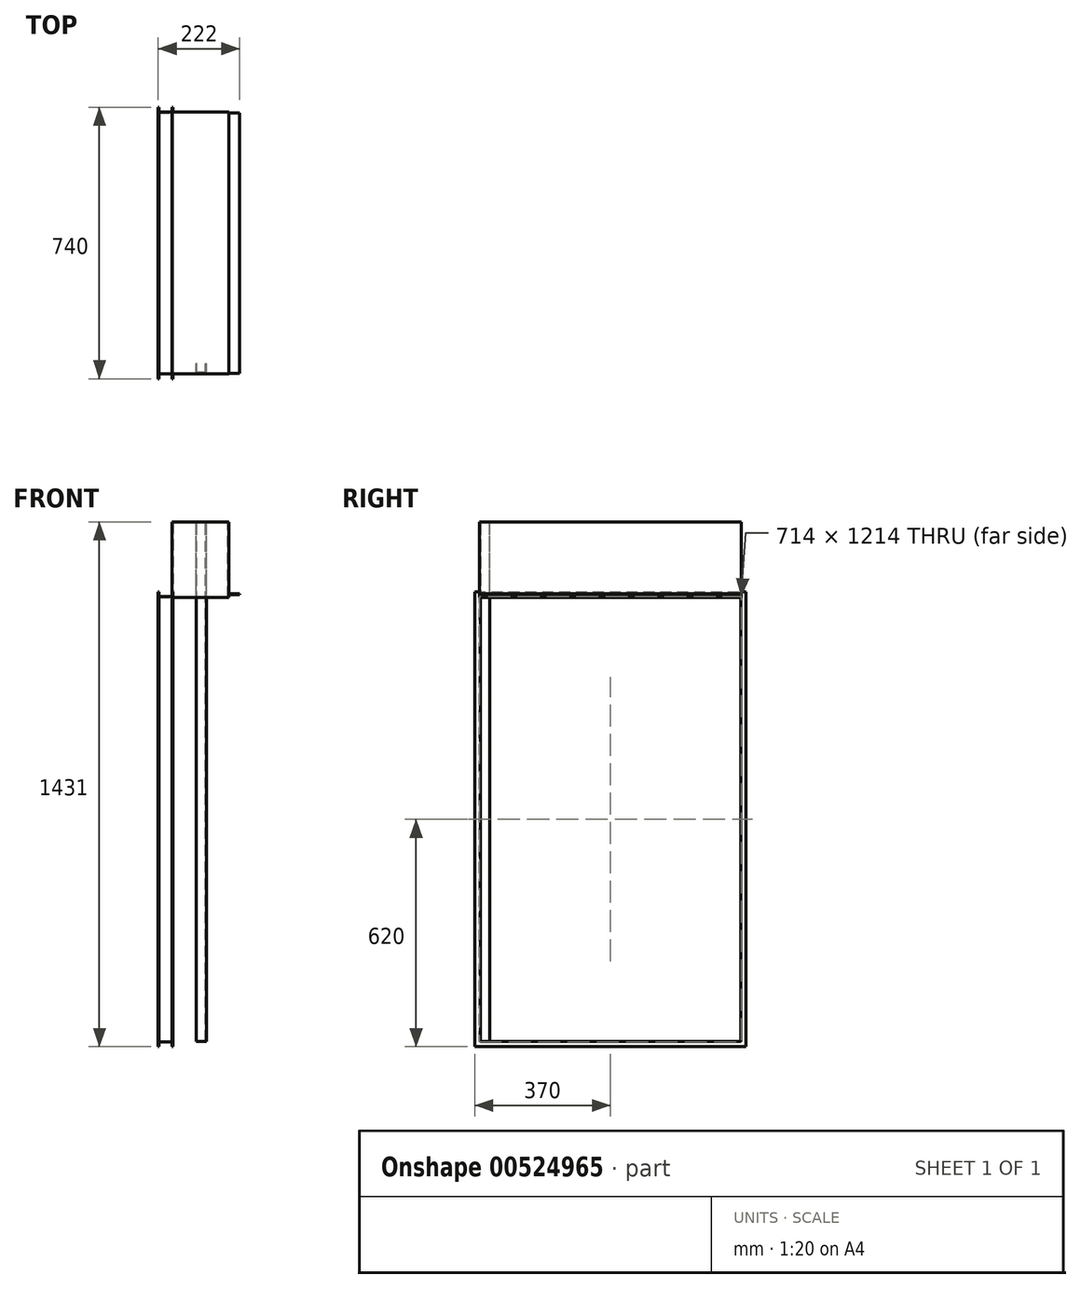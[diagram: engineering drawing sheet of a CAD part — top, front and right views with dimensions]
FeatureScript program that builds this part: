
annotation { "Feature Type Name" : "Feature", "Feature Type Description" : "" }
export const myFeature = defineFeature(function(context is Context, id is Id, definition is map)
    precondition{}
    {
        {
            var Q0;
            Q0=qCreatedBy(makeId("Front.planeOp"),FACE);
            var sketch = newSketch(context, id + "F0", { "sketchPlane" : qUnion([Q0])});
            skLineSegment(sketch, "E0", {"start": v(0, 0) * mm, "end": v(0, 206) * mm});
            skLineSegment(sketch, "E1", {"start": v(0, 206) * mm, "end": v(-154, 206) * mm});
            skLineSegment(sketch, "E2", {"start": v(-154, 206) * mm, "end": v(-154, 0) * mm});
            skLineSegment(sketch, "E3", {"start": v(0, 10) * mm, "end": v(30, 10) * mm});
            skLineSegment(sketch, "E4.0", {"start": v(-152, 204) * mm, "end": v(-152, 0) * mm});
            skLineSegment(sketch, "E4.1", {"start": v(-2, 204) * mm, "end": v(-152, 204) * mm});
            skLineSegment(sketch, "E4.2", {"start": v(-2, 0) * mm, "end": v(-2, 204) * mm});
            skLineSegment(sketch, "E5.0", {"start": v(0, 8) * mm, "end": v(30, 8) * mm});
            skLineSegment(sketch, "E6", {"start": v(-154, 0) * mm, "end": v(-152, 0) * mm});
            skLineSegment(sketch, "E7", {"start": v(30, 8) * mm, "end": v(30, 10) * mm});
            skLineSegment(sketch, "E8", {"start": v(-2, 0) * mm, "end": v(0, 0) * mm});
            skPoint(sketch, "E9.start.orphan", {"position": v(-150, -15) * mm});
            skPoint(sketch, "E10.start.orphan", {"position": v(-190, -15) * mm});
            skSolve(sketch);
        }
        {
            var Q0;
            {var subQ3=sQuery(id+"F0.wireOp",EDGE,"E1");Q0=makeQuery(id+"F0.imprint","IMPRINT",FACE,{"disambiguationData":[TD([[makeQuery(id+"F0.imprint","IMPRINT",EDGE,{"derivedFrom":subQ3}),1.0]])]});}
            var Q1;
            {var subQ0=sQuery(id+"F0.wireOp",EDGE,"E3");Q1=makeQuery(id+"F0.imprint","IMPRINT",FACE,{"disambiguationData":[TD([[makeQuery(id+"F0.imprint","IMPRINT",EDGE,{"derivedFrom":subQ0}),-1.0]])]});}
            extrude(context, id + "F1", {"entities" : qUnion([Q0, Q1]), "oppositeDirection" : true, "depth" : 710 * mm, "offsetDistance" : 25 * mm});
        }
        {
            var Q0;
            Q0=makeQuery(id+"F1.opExtrude","SWEPT_FACE",FACE,{"disambiguationData":[OSD([sQuery(id+"F0.wireOp",EDGE,"E4.0")])]});
            cPlane(context, id + "F2", {"entities" : qUnion([Q0]), "cplaneType" : CPlaneType.OFFSET, "offset" : 0 * mm, "width" : 150 * mm, "height" : 150 * mm});
        }
        {
            var Q0;
            Q0=qCreatedBy(id+"F2.planeOp",FACE);
            var sketch = newSketch(context, id + "F3", { "sketchPlane" : qUnion([Q0])});
            skLineSegment(sketch, "E11.bottom", {"start": v(0, 0) * mm, "end": v(710, 0) * mm});
            skLineSegment(sketch, "E11.top", {"start": v(0, -1210) * mm, "end": v(710, -1210) * mm});
            skLineSegment(sketch, "E11.left", {"start": v(0, 0) * mm, "end": v(0, -1210) * mm});
            skLineSegment(sketch, "E11.right", {"start": v(710, 0) * mm, "end": v(710, -1210) * mm});
            skSolve(sketch);
        }
        {
            var Q0;
            {var subQ0=sQuery(id+"F0.wireOp",EDGE,"E1");Q0=makeQuery(id+"F0.imprint","IMPRINT",FACE,{"disambiguationData":[TD([[makeQuery(id+"F0.imprint","IMPRINT",EDGE,{"derivedFrom":subQ0}),1.0]])]});}
            cPlane(context, id + "F4", {"entities" : qUnion([Q0]), "cplaneType" : CPlaneType.OFFSET, "offset" : 0 * mm, "width" : 150 * mm, "height" : 150 * mm});
        }
        {
            var Q0;
            Q0=qCreatedBy(id+"F4.planeOp",FACE);
            var sketch = newSketch(context, id + "F5", { "sketchPlane" : qUnion([Q0])});
            skLineSegment(sketch, "E12", {"start": v(-152, 0) * mm, "end": v(-152, 15) * mm});
            skLineSegment(sketch, "E13", {"start": v(-192, 15) * mm, "end": v(-192, 0) * mm});
            skLineSegment(sketch, "E14", {"start": v(-192, 0) * mm, "end": v(-152, 0) * mm});
            skLineSegment(sketch, "E15.0", {"start": v(-154, 2) * mm, "end": v(-154, 15) * mm});
            skLineSegment(sketch, "E15.1", {"start": v(-190, 2) * mm, "end": v(-154, 2) * mm});
            skLineSegment(sketch, "E15.2", {"start": v(-190, 15) * mm, "end": v(-190, 2) * mm});
            skLineSegment(sketch, "E16", {"start": v(-192, 15) * mm, "end": v(-190, 15) * mm});
            skLineSegment(sketch, "E17", {"start": v(-154, 15) * mm, "end": v(-152, 15) * mm});
            skSolve(sketch);
        }
        {
            var Q0;
            Q0=makeQuery(id+"F5.imprint","IMPRINT",FACE,{"disambiguationData":[TD([[makeQuery(id+"F5.imprint","IMPRINT",EDGE,{"derivedFrom":sQuery(id+"F5.wireOp",EDGE,"E12")}),1.0]])]});
            var Q1;
            Q1 = qConstructionFilter(qBodyType(qCreatedBy(id + "F3" ,EDGE), BodyType.WIRE), ConstructionObject.NO);
            sweep(context, id + "F6", {"operationType" : NewBodyOperationType.ADD, "profiles" : qUnion([Q0]), "path" : qUnion([Q1])});
        }
        {
            var Q0;
            Q0=makeQuery(id+"F1.opExtrude","SWEPT_FACE",FACE,{"disambiguationData":[OSD([sQuery(id+"F0.wireOp",EDGE,"E4.1")])]});
            var sketch = newSketch(context, id + "F7", { "sketchPlane" : qUnion([Q0])});
            skLineSegment(sketch, "E18.bottom", {"start": v(-77, 0) * mm, "end": v(-89, 0) * mm});
            skLineSegment(sketch, "E18.top", {"start": v(-87, -26) * mm, "end": v(-89, -26) * mm});
            skLineSegment(sketch, "E18.right", {"start": v(-89, 0) * mm, "end": v(-89, -26) * mm});
            skLineSegment(sketch, "E19.MirrorCS", {"start": v(-63, -26) * mm, "end": v(-61, -26) * mm});
            skLineSegment(sketch, "E20.MirrorCS", {"start": v(-61, 0) * mm, "end": v(-61, -26) * mm});
            skLineSegment(sketch, "E21.MirrorCS", {"start": v(-75, 0) * mm, "end": v(-61, 0) * mm});
            skLineSegment(sketch, "E22.0", {"start": v(-87, -2) * mm, "end": v(-87, -26) * mm});
            skLineSegment(sketch, "E22.1", {"start": v(-75, -2) * mm, "end": v(-87, -2) * mm});
            skLineSegment(sketch, "E22.2", {"start": v(-75, -2) * mm, "end": v(-63, -2) * mm});
            skLineSegment(sketch, "E22.3", {"start": v(-63, -2) * mm, "end": v(-63, -26) * mm});
            skPoint(sketch, "E23.orphan", {"position": v(-75, -26) * mm});
            skSolve(sketch);
        }
        {
            var Q0;
            Q0=makeQuery(id+"F7.imprint","IMPRINT",FACE,{"disambiguationData":[TD([[makeQuery(id+"F7.imprint","IMPRINT",EDGE,{"derivedFrom":sQuery(id+"F7.wireOp",EDGE,"E18.bottom")}),1.0]])]});
            var Q1;
            Q1=makeQuery(id+"F6.opSweep","SWEPT_FACE",FACE,{"disambiguationData":[OSD([sQuery(id+"F3.wireOp",EDGE,"E11.top"),sQuery(id+"F5.wireOp",EDGE,"LKxghPaX-kVdG-r2eD-1wmU-N69SjMgiJEC4")])]});
            extrude(context, id + "F8", {"entities" : qUnion([Q0]), "operationType" : NewBodyOperationType.ADD, "endBound" : BoundingType.UP_TO_SURFACE, "depth" : 1200 * mm, "endBoundEntityFace" : qUnion([Q1]), "offsetDistance" : 25 * mm});
        }
        {
            var Q0;
            {var subQ0=sQuery(id+"F0.wireOp",EDGE,"E4.1");Q0=makeQuery(id+"F8.boolean.opBoolean","MERGE",FACE,{"derivedFrom":[makeQuery(id+"F1.opExtrude","CAP_FACE",FACE,{"disambiguationData":[OSD([sQuery(id+"F0.wireOp",EDGE,"E0"),sQuery(id+"F0.wireOp",EDGE,"E1"),sQuery(id+"F0.wireOp",EDGE,"E2"),sQuery(id+"F0.wireOp",EDGE,"E3"),sQuery(id+"F0.wireOp",EDGE,"E4.0"),subQ0,sQuery(id+"F0.wireOp",EDGE,"E4.2"),sQuery(id+"F0.wireOp",EDGE,"E5.0"),sQuery(id+"F0.wireOp",EDGE,"E6"),sQuery(id+"F0.wireOp",EDGE,"E7"),sQuery(id+"F0.wireOp",EDGE,"E8")])],"isStart":true}),makeQuery(id+"F8.opExtrude","SWEPT_FACE",FACE,{"disambiguationData":[OSD([subQ0,sQuery(id+"F7.wireOp",EDGE,"E18.bottom"),sQuery(id+"F7.wireOp",EDGE,"E21.MirrorCS")])]})]});}
            var sketch = newSketch(context, id + "F9", { "sketchPlane" : qUnion([Q0])});
            skLineSegment(sketch, "E24.bottom", {"start": v(-154, 206) * mm, "end": v(0, 206) * mm});
            skLineSegment(sketch, "E24.top", {"start": v(-154, 0) * mm, "end": v(0, 0) * mm});
            skLineSegment(sketch, "E24.left", {"start": v(-154, 206) * mm, "end": v(-154, 0) * mm});
            skLineSegment(sketch, "E24.right", {"start": v(0, 206) * mm, "end": v(0, 0) * mm});
            skSolve(sketch);
        }
        {
            var Q0;
            Q0 = qSketchRegion(id + "F9", true);
            extrude(context, id + "F10", {"entities" : qUnion([Q0]), "operationType" : NewBodyOperationType.ADD, "depth" : 2 * mm, "offsetDistance" : 25 * mm});
        }
        {
            var Q0;
            Q0=makeQuery(id+"F1.opExtrude","CAP_FACE",FACE,{"disambiguationData":[OSD([sQuery(id+"F0.wireOp",EDGE,"E0"),sQuery(id+"F0.wireOp",EDGE,"E1"),sQuery(id+"F0.wireOp",EDGE,"E2"),sQuery(id+"F0.wireOp",EDGE,"E3"),sQuery(id+"F0.wireOp",EDGE,"E4.0"),sQuery(id+"F0.wireOp",EDGE,"E4.1"),sQuery(id+"F0.wireOp",EDGE,"E4.2"),sQuery(id+"F0.wireOp",EDGE,"E5.0"),sQuery(id+"F0.wireOp",EDGE,"E6"),sQuery(id+"F0.wireOp",EDGE,"E7"),sQuery(id+"F0.wireOp",EDGE,"E8")])],"isStart":false});
            var sketch = newSketch(context, id + "F11", { "sketchPlane" : qUnion([Q0])});
            skLineSegment(sketch, "E25.bottom", {"start": v(154, 206) * mm, "end": v(0, 206) * mm});
            skLineSegment(sketch, "E25.top", {"start": v(154, 0) * mm, "end": v(0, 0) * mm});
            skLineSegment(sketch, "E25.left", {"start": v(154, 206) * mm, "end": v(154, 0) * mm});
            skLineSegment(sketch, "E25.right", {"start": v(0, 206) * mm, "end": v(0, 0) * mm});
            skSolve(sketch);
        }
        {
            var Q0;
            Q0 = qSketchRegion(id + "F11", true);
            extrude(context, id + "F12", {"entities" : qUnion([Q0]), "operationType" : NewBodyOperationType.ADD, "depth" : 2 * mm, "offsetDistance" : 25 * mm});
        }
    });
